# Revit family: P191568KX-121c_KFEG500
name_source: partatom
category: Specialty Equipment
units: mm (PartAtom-declared; Revit-internal decimal feet)

## family parameters
Always vertical = Yes
Cut with Voids When Loaded = No
Enable Cutting in Views = No
Maintain Annotation Orientation = No
Part Type = Normal
Room Calculation Point = No
Round Connector Dimension = Use Diameter
Shared = No
Work Plane-Based = No

## types (3) — shared parameters
Amps = 0 A
Clearance Material = ARCAT - Clearance
Cooktop Material = ARCAT - Glass - Tempered - Black
Default Elevation = 0"
Depth = 27 3/4"
Family Name = COOKING
Glass Material = ARCAT - Glass - Black
Handle Material = ARCAT - Metal - Steel - Gray
Height = 47 1/8"
Knob Material = ARCAT - Metal - Steel - Gray
Leg Material = ARCAT - Plastic - Black
Manufacturer = KitchenAid
Voltage = 0 V
Width = 29 15/16"

## per-type parameters (varying)
| type | Body Material | Display Panel Material | Door Material |
| KFEG500SS | ARCAT - Metal - Steel - Black | ARCAT - Glass - Black | ARCAT - Metal - Steel - Stainless |
| KFEG500BS | ARCAT - Metal - Steel - Black | ARCAT - Glass - Black | ARCAT - Metal - Steel - Black Stainless |
| KFEG500WH | ARCAT - Metal - Steel - White | ARCAT - Glass - White | ARCAT - Metal - Steel - White |

note: column(s) folded — value = type name in every type: Model

## geometry (parser evidence)
native form markers: Sweep x6
no freeform markers — native parametric forms only
